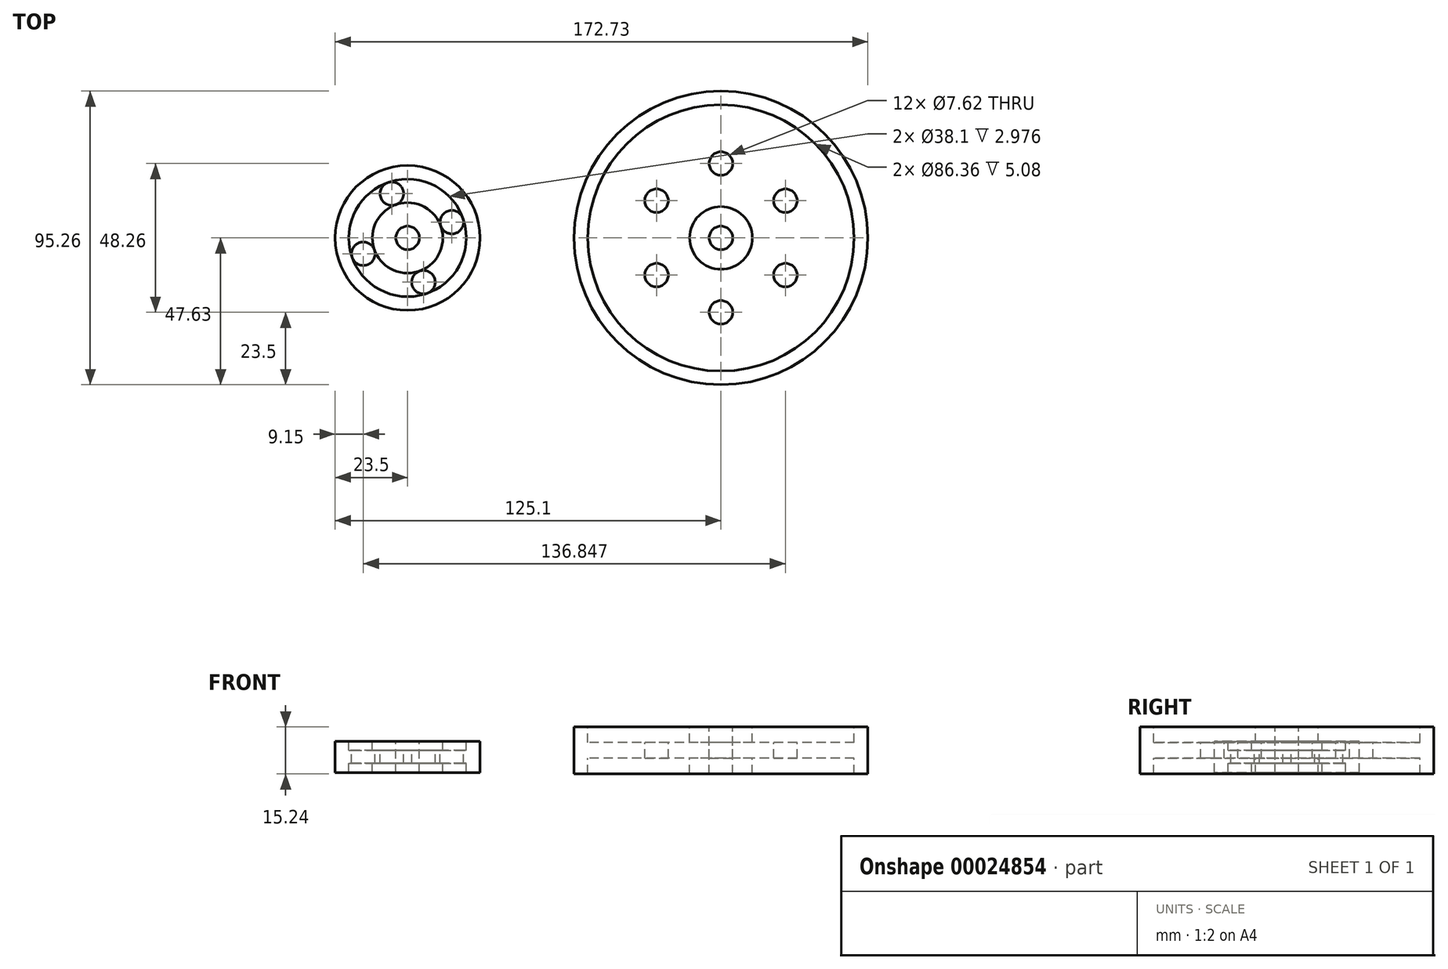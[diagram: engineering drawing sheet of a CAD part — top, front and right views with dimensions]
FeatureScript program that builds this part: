
annotation { "Feature Type Name" : "Feature", "Feature Type Description" : "" }
export const myFeature = defineFeature(function(context is Context, id is Id, definition is map)
    precondition{}
    {
        {
            var Q0;
            Q0=qCreatedBy(makeId("Front.planeOp"),FACE);
            var sketch = newSketch(context, id + "F0", { "sketchPlane" : qUnion([Q0])});
            skLineSegment(sketch, "E0", {"start": v(0, 27.04) * mm, "end": v(0, -25.42) * mm, "construction": true});
            skLineSegment(sketch, "E1.bottom", {"start": v(3.81, 7.6) * mm, "end": v(10.16, 7.6) * mm});
            skLineSegment(sketch, "E1.top", {"start": v(3.81, -7.64) * mm, "end": v(10.16, -7.64) * mm});
            skLineSegment(sketch, "E1.left", {"start": v(3.8, 7.6) * mm, "end": v(3.8, -7.64) * mm});
            skLineSegment(sketch, "E2", {"start": v(10.16, 7.6) * mm, "end": v(10.16, 2.52) * mm});
            skLineSegment(sketch, "E3", {"start": v(10.16, 2.52) * mm, "end": v(43.18, 2.52) * mm});
            skLineSegment(sketch, "E4", {"start": v(43.18, 2.52) * mm, "end": v(43.18, 7.6) * mm});
            skLineSegment(sketch, "E5", {"start": v(43.18, 7.6) * mm, "end": v(47.63, 7.6) * mm});
            skLineSegment(sketch, "E6", {"start": v(47.63, 7.6) * mm, "end": v(47.63, -7.64) * mm});
            skLineSegment(sketch, "E7", {"start": v(47.63, -7.64) * mm, "end": v(43.18, -7.64) * mm});
            skLineSegment(sketch, "E8", {"start": v(43.18, -7.64) * mm, "end": v(43.18, -2.56) * mm});
            skLineSegment(sketch, "E9", {"start": v(43.18, -2.56) * mm, "end": v(10.16, -2.56) * mm});
            skLineSegment(sketch, "E10", {"start": v(10.16, -2.56) * mm, "end": v(10.16, -7.64) * mm});
            skSolve(sketch);
        }
        {
            var Q0;
            Q0=makeQuery(id+"F0.imprint","IMPRINT",FACE,{"disambiguationData":[TD([[makeQuery(id+"F0.imprint","IMPRINT",EDGE,{"derivedFrom":sQuery(id+"F0.wireOp",EDGE,"E1.bottom")}),-1.0]])]});
            var Q1;
            Q1=sQuery(id+"F0.wireOp",EDGE,"E0");
            revolve(context, id + "F1", {"entities" : qUnion([Q0]), "axis" : qUnion([Q1]), "revolveType" : RevolveType.FULL});
        }
        {
            var Q0;
            Q0=makeQuery(id+"F1.opRevolve","SWEPT_FACE",FACE,{"disambiguationData":[OSD([sQuery(id+"F0.wireOp",EDGE,"E3")])]});
            var sketch = newSketch(context, id + "F2", { "sketchPlane" : qUnion([Q0])});
            skCircle(sketch, "E11", {"center": v(0, 24.13) * mm, "radius": 3.8 * mm});
            skCircle(sketch, "E12.1.0", {"center": v(-20.9, 12.07) * mm, "radius": 3.8 * mm});
            skCircle(sketch, "E12.2.0", {"center": v(-20.9, -12.06) * mm, "radius": 3.8 * mm});
            skCircle(sketch, "E12.3.0", {"center": v(0, -24.13) * mm, "radius": 3.8 * mm});
            skCircle(sketch, "E12.4.0", {"center": v(20.9, -12.07) * mm, "radius": 3.8 * mm});
            skCircle(sketch, "E12.5.0", {"center": v(20.9, 12.07) * mm, "radius": 3.8 * mm});
            skPoint(sketch, "E12.center", {"position": v(0, 0) * mm});
            skSolve(sketch);
        }
        {
            var Q0;
            Q0=makeQuery(id+"F2.imprint","IMPRINT",FACE,{"disambiguationData":[TD([[makeQuery(id+"F2.imprint","IMPRINT",EDGE,{"derivedFrom":sQuery(id+"F2.wireOp",EDGE,"E11")}),1.0]])]});
            var Q1;
            Q1=makeQuery(id+"F2.imprint","IMPRINT",FACE,{"disambiguationData":[TD([[makeQuery(id+"F2.imprint","IMPRINT",EDGE,{"derivedFrom":sQuery(id+"F2.wireOp",EDGE,"E12.1.0")}),1.0]])]});
            var Q2;
            Q2=makeQuery(id+"F2.imprint","IMPRINT",FACE,{"disambiguationData":[TD([[makeQuery(id+"F2.imprint","IMPRINT",EDGE,{"derivedFrom":sQuery(id+"F2.wireOp",EDGE,"E12.2.0")}),1.0]])]});
            var Q3;
            Q3=makeQuery(id+"F2.imprint","IMPRINT",FACE,{"disambiguationData":[TD([[makeQuery(id+"F2.imprint","IMPRINT",EDGE,{"derivedFrom":sQuery(id+"F2.wireOp",EDGE,"E12.3.0")}),1.0]])]});
            var Q4;
            Q4=makeQuery(id+"F2.imprint","IMPRINT",FACE,{"disambiguationData":[TD([[makeQuery(id+"F2.imprint","IMPRINT",EDGE,{"derivedFrom":sQuery(id+"F2.wireOp",EDGE,"E12.4.0")}),1.0]])]});
            var Q5;
            Q5=makeQuery(id+"F2.imprint","IMPRINT",FACE,{"disambiguationData":[TD([[makeQuery(id+"F2.imprint","IMPRINT",EDGE,{"derivedFrom":sQuery(id+"F2.wireOp",EDGE,"E12.5.0")}),1.0]])]});
            extrude(context, id + "F3", {"entities" : qUnion([Q0, Q1, Q2, Q3, Q4, Q5]), "operationType" : NewBodyOperationType.REMOVE, "endBound" : BoundingType.THROUGH_ALL, "oppositeDirection" : true, "depth" : 25.4 * mm});
        }
        {
            var Q0;
            Q0=qCreatedBy(makeId("Front.planeOp"),FACE);
            var sketch = newSketch(context, id + "F4", { "sketchPlane" : qUnion([Q0])});
            skLineSegment(sketch, "E13", {"start": v(-101.6, 14.7) * mm, "end": v(-101.6, -25.2) * mm, "construction": true});
            skLineSegment(sketch, "E14.bottom", {"start": v(-97.8, 2.98) * mm, "end": v(-90.17, 2.98) * mm});
            skLineSegment(sketch, "E14.top", {"start": v(-97.8, -7.18) * mm, "end": v(-90.17, -7.18) * mm});
            skLineSegment(sketch, "E14.left", {"start": v(-97.8, 2.98) * mm, "end": v(-97.8, -7.18) * mm});
            skLineSegment(sketch, "E15", {"start": v(-90.17, 2.98) * mm, "end": v(-90.17, 0) * mm});
            skLineSegment(sketch, "E16", {"start": v(-90.17, 0) * mm, "end": v(-82.55, 0) * mm});
            skLineSegment(sketch, "E17", {"start": v(-82.55, 0) * mm, "end": v(-82.55, 2.98) * mm});
            skLineSegment(sketch, "E18", {"start": v(-82.55, 2.98) * mm, "end": v(-78.1, 2.98) * mm});
            skLineSegment(sketch, "E19", {"start": v(-78.1, 2.98) * mm, "end": v(-78.1, -7.18) * mm});
            skLineSegment(sketch, "E20", {"start": v(-78.1, -7.18) * mm, "end": v(-82.55, -7.18) * mm});
            skLineSegment(sketch, "E21", {"start": v(-82.55, -7.18) * mm, "end": v(-82.55, -4.2) * mm});
            skLineSegment(sketch, "E22", {"start": v(-82.55, -4.2) * mm, "end": v(-90.17, -4.2) * mm});
            skLineSegment(sketch, "E23", {"start": v(-90.17, -4.2) * mm, "end": v(-90.17, -7.18) * mm});
            skSolve(sketch);
        }
        {
            var Q0;
            Q0=makeQuery(id+"F4.imprint","IMPRINT",FACE,{"disambiguationData":[TD([[makeQuery(id+"F4.imprint","IMPRINT",EDGE,{"derivedFrom":sQuery(id+"F4.wireOp",EDGE,"E14.bottom")}),-1.0]])]});
            var Q1;
            Q1=sQuery(id+"F4.wireOp",EDGE,"E13");
            revolve(context, id + "F5", {"entities" : qUnion([Q0]), "axis" : qUnion([Q1]), "revolveType" : RevolveType.FULL});
        }
        {
            var Q0;
            Q0=makeQuery(id+"F5.opRevolve","SWEPT_FACE",FACE,{"disambiguationData":[OSD([sQuery(id+"F4.wireOp",EDGE,"E16")])]});
            var sketch = newSketch(context, id + "F6", { "sketchPlane" : qUnion([Q0])});
            skCircle(sketch, "E24.0", {"center": v(-101.6, 0) * mm, "radius": 3.8 * mm});
            skCircle(sketch, "E25.1", {"center": v(-101.6, 0) * mm, "radius": 11.43 * mm});
            skCircle(sketch, "E26.2", {"center": v(-101.6, 0) * mm, "radius": 19.05 * mm});
            skCircle(sketch, "E27", {"center": v(-87.25, 5.13) * mm, "radius": 3.81 * mm});
            skCircle(sketch, "E28.1.0", {"center": v(-106.73, 14.35) * mm, "radius": 3.81 * mm});
            skCircle(sketch, "E28.2.0", {"center": v(-115.95, -5.13) * mm, "radius": 3.81 * mm});
            skCircle(sketch, "E28.3.0", {"center": v(-96.47, -14.35) * mm, "radius": 3.81 * mm});
            skSolve(sketch);
        }
        {
            var Q0;
            {var subQ0=sQuery(id+"F6.wireOp",EDGE,"E27");var subQ2=makeQuery(id+"F6.imprint","INTERSECT",VERTEX,{"derivedFrom":[sQuery(id+"F6.wireOp",EDGE,"E26.2"),subQ0]});Q0=makeQuery(id+"F6.imprint","IMPRINT",FACE,{"disambiguationData":[TD([[makeQuery(id+"F6.imprint","IMPRINT",EDGE,{"disambiguationData":[TD([[subQ2,-1.0]])],"derivedFrom":subQ0}),1.0]])]});}
            var Q1;
            {var subQ0=sQuery(id+"F6.wireOp",EDGE,"E28.1.0");var subQ2=makeQuery(id+"F6.imprint","INTERSECT",VERTEX,{"derivedFrom":[sQuery(id+"F6.wireOp",EDGE,"E26.2"),subQ0]});Q1=makeQuery(id+"F6.imprint","IMPRINT",FACE,{"disambiguationData":[TD([[makeQuery(id+"F6.imprint","IMPRINT",EDGE,{"disambiguationData":[TD([[subQ2,-1.0]])],"derivedFrom":subQ0}),1.0]])]});}
            var Q2;
            {var subQ0=sQuery(id+"F6.wireOp",EDGE,"E28.2.0");var subQ2=makeQuery(id+"F6.imprint","INTERSECT",VERTEX,{"derivedFrom":[sQuery(id+"F6.wireOp",EDGE,"E26.2"),subQ0]});Q2=makeQuery(id+"F6.imprint","IMPRINT",FACE,{"disambiguationData":[TD([[makeQuery(id+"F6.imprint","IMPRINT",EDGE,{"disambiguationData":[TD([[subQ2,-1.0]])],"derivedFrom":subQ0}),1.0]])]});}
            var Q3;
            {var subQ0=sQuery(id+"F6.wireOp",EDGE,"E28.3.0");var subQ2=makeQuery(id+"F6.imprint","INTERSECT",VERTEX,{"derivedFrom":[sQuery(id+"F6.wireOp",EDGE,"E26.2"),subQ0]});Q3=makeQuery(id+"F6.imprint","IMPRINT",FACE,{"disambiguationData":[TD([[makeQuery(id+"F6.imprint","IMPRINT",EDGE,{"disambiguationData":[TD([[subQ2,-1.0]])],"derivedFrom":subQ0}),1.0]])]});}
            extrude(context, id + "F7", {"entities" : qUnion([Q0, Q1, Q2, Q3]), "operationType" : NewBodyOperationType.REMOVE, "endBound" : BoundingType.THROUGH_ALL, "oppositeDirection" : true, "depth" : 25.4 * mm});
        }
    });
